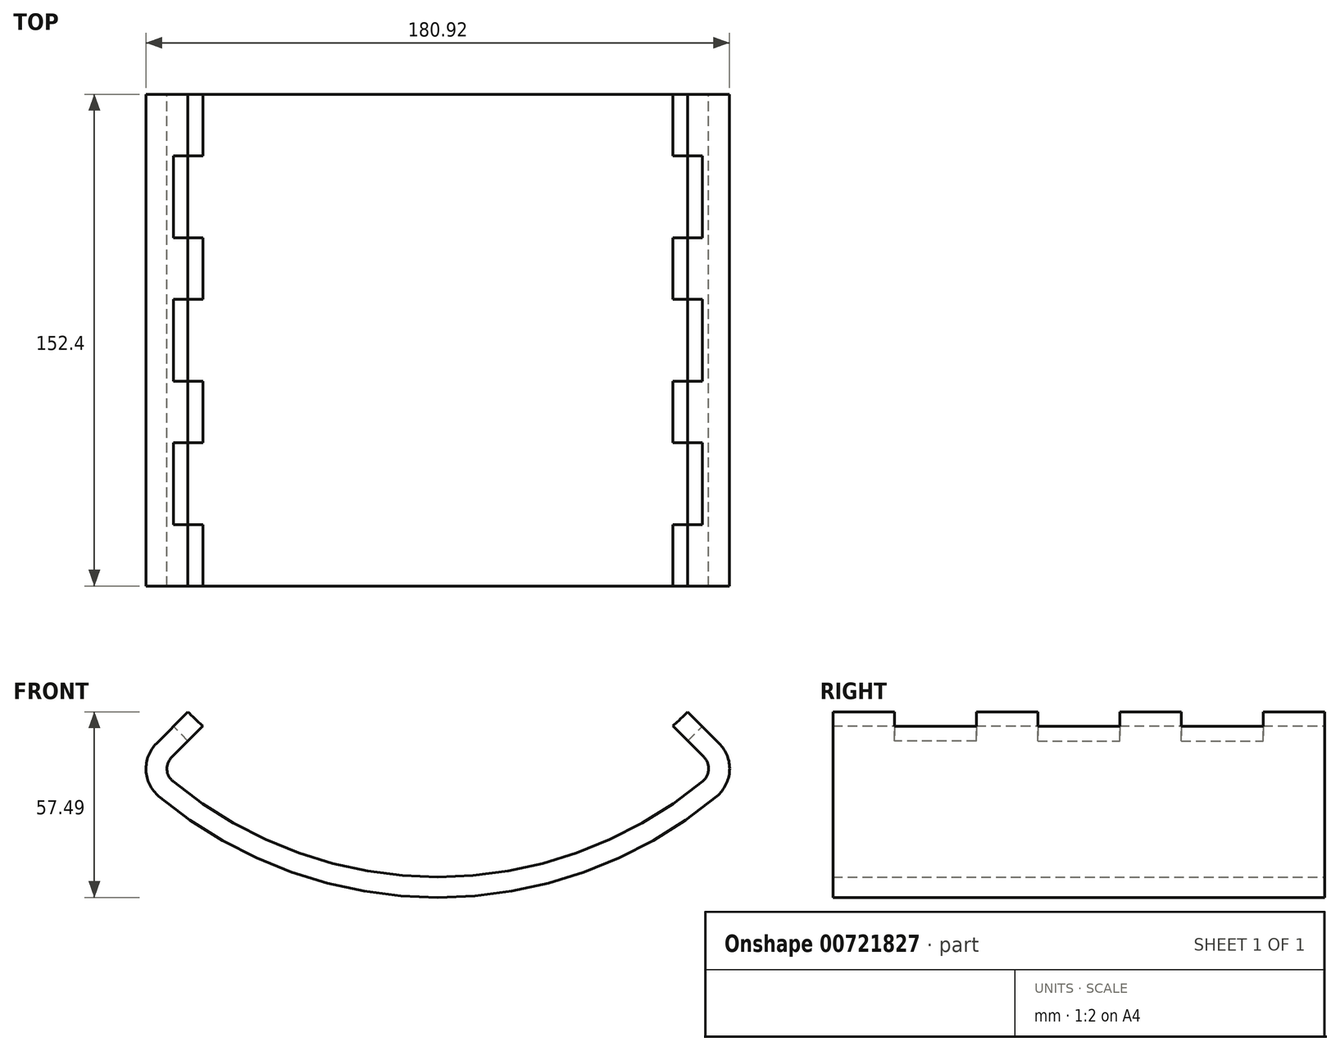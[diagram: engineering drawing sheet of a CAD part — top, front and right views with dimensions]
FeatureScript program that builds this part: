
annotation { "Feature Type Name" : "Feature", "Feature Type Description" : "" }
export const myFeature = defineFeature(function(context is Context, id is Id, definition is map)
    precondition{}
    {
        {
            var Q0;
            Q0=qCreatedBy(makeId("Front.planeOp"),FACE);
            var sketch = newSketch(context, id + "F0", { "sketchPlane" : qUnion([Q0])});
            skArc(sketch, "E0", {"start": v(-85.5, -96.04) * mm, "mid": v(0, -128.59) * mm, "end": v(85.5, -96.04) * mm});
            skArc(sketch, "E1", {"start": v(-95.42, -95.42) * mm, "mid": v(0, -134.94) * mm, "end": v(95.42, -95.42) * mm});
            skArc(sketch, "E2", {"start": v(-77.45, -77.45) * mm, "mid": v(-75.18, -79.67) * mm, "end": v(-72.83, -81.81) * mm});
            skArc(sketch, "E3.trimOffspring", {"start": v(72.83, -81.81) * mm, "mid": v(75.35, -79.5) * mm, "end": v(77.79, -77.12) * mm});
            skLineSegment(sketch, "E4", {"start": v(-77.45, -77.45) * mm, "end": v(-95.42, -95.42) * mm});
            skLineSegment(sketch, "E5", {"start": v(-72.83, -81.81) * mm, "end": v(-86.32, -95.3) * mm});
            skLineSegment(sketch, "E6", {"start": v(72.83, -81.81) * mm, "end": v(86.32, -95.3) * mm});
            skLineSegment(sketch, "E7", {"start": v(77.45, -77.45) * mm, "end": v(95.42, -95.42) * mm});
            skArc(sketch, "E8", {"start": v(-86.32, -95.3) * mm, "mid": v(0, -128.59) * mm, "end": v(86.32, -95.3) * mm});
            skArc(sketch, "E9.trimOffspring", {"start": v(-91.03, -90.82) * mm, "mid": v(-90.98, -90.87) * mm, "end": v(-90.93, -90.93) * mm});
            skSolve(sketch);
        }
        {
            var Q0;
            Q0 = qSketchRegion(id + "F0", true);
            extrude(context, id + "F1", {"entities" : qUnion([Q0]), "depth" : 152.4 * mm, "offsetDistance" : 25.4 * mm, "symmetric" : true});
        }
        {
            var Q0;
            Q0=makeQuery(id+"F1.opExtrude","SWEPT_EDGE",EDGE,{"disambiguationData":[OSD([sQuery(id+"F0.wireOp",EDGE,"E1"),sQuery(id+"F0.wireOp",EDGE,"b23c7c19-87c6-4823-a1c1-1b1030b646d8.trimOffspring")])]});
            var Q1;
            Q1=makeQuery(id+"F1.opExtrude","SWEPT_EDGE",EDGE,{"disambiguationData":[OSD([sQuery(id+"F0.wireOp",EDGE,"E1"),sQuery(id+"F0.wireOp",EDGE,"43c429cb-6016-4fc4-948b-cda1806fe1c8.trimOffspring")])]});
            fillet(context, id + "F2", {"entities" : qUnion([Q0, Q1]), "radius" : 11.1 * mm, "tangentPropagation" : true, "allowEdgeOverflow" : false});
        }
        {
            var Q0;
            Q0=makeQuery(id+"F1.opExtrude","SWEPT_EDGE",EDGE,{"disambiguationData":[OSD([sQuery(id+"F0.wireOp",EDGE,"E5"),sQuery(id+"F0.wireOp",EDGE,"E8")])]});
            var Q1;
            Q1=makeQuery(id+"F1.opExtrude","SWEPT_EDGE",EDGE,{"disambiguationData":[OSD([sQuery(id+"F0.wireOp",EDGE,"E6"),sQuery(id+"F0.wireOp",EDGE,"E8")])]});
            fillet(context, id + "F3", {"entities" : qUnion([Q0, Q1]), "radius" : 5.08 * mm, "tangentPropagation" : true, "allowEdgeOverflow" : false});
        }
        {
            var Q0;
            Q0=makeQuery(id+"F1.opExtrude","SWEPT_FACE",FACE,{"disambiguationData":[OSD([sQuery(id+"F0.wireOp",EDGE,"E7")])]});
            var sketch = newSketch(context, id + "F4", { "sketchPlane" : qUnion([Q0])});
            skLineSegment(sketch, "E10.bottom", {"start": v(-57.15, -106.28) * mm, "end": v(-31.75, -106.28) * mm});
            skLineSegment(sketch, "E10.top", {"start": v(-57.15, -115.89) * mm, "end": v(-31.75, -115.89) * mm});
            skLineSegment(sketch, "E10.left", {"start": v(-57.15, -106.28) * mm, "end": v(-57.15, -115.89) * mm});
            skLineSegment(sketch, "E10.right", {"start": v(-31.75, -106.28) * mm, "end": v(-31.75, -115.89) * mm});
            skLineSegment(sketch, "E11.MirrorCS", {"start": v(31.75, -106.28) * mm, "end": v(31.75, -115.89) * mm});
            skLineSegment(sketch, "E12.MirrorCS", {"start": v(57.15, -106.28) * mm, "end": v(31.75, -106.28) * mm});
            skLineSegment(sketch, "E13.MirrorCS", {"start": v(57.15, -115.89) * mm, "end": v(31.75, -115.89) * mm});
            skLineSegment(sketch, "E14.MirrorCS", {"start": v(57.15, -106.28) * mm, "end": v(57.15, -115.89) * mm});
            skLineSegment(sketch, "E15.bottom", {"start": v(-12.7, -105.34) * mm, "end": v(12.7, -105.34) * mm});
            skLineSegment(sketch, "E15.top", {"start": v(-12.7, -115.89) * mm, "end": v(12.7, -115.89) * mm});
            skLineSegment(sketch, "E15.left", {"start": v(-12.7, -105.34) * mm, "end": v(-12.7, -115.89) * mm});
            skLineSegment(sketch, "E15.right", {"start": v(12.7, -105.34) * mm, "end": v(12.7, -115.89) * mm});
            skSolve(sketch);
        }
        {
            var Q0;
            Q0 = qSketchRegion(id + "F4", true);
            extrude(context, id + "F5", {"entities" : qUnion([Q0]), "operationType" : NewBodyOperationType.REMOVE, "oppositeDirection" : true, "depth" : 25.4 * mm, "offsetDistance" : 25.4 * mm});
        }
        {
            var Q0;
            Q0=makeQuery(id+"F1.opExtrude","SWEPT_FACE",FACE,{"disambiguationData":[OSD([sQuery(id+"F0.wireOp",EDGE,"E4")])]});
            var sketch = newSketch(context, id + "F6", { "sketchPlane" : qUnion([Q0])});
            skLineSegment(sketch, "E16.bottom", {"start": v(-57.15, -103.22) * mm, "end": v(-31.75, -103.22) * mm});
            skLineSegment(sketch, "E16.top", {"start": v(-57.15, -115.89) * mm, "end": v(-31.75, -115.89) * mm});
            skLineSegment(sketch, "E16.left", {"start": v(-57.15, -103.22) * mm, "end": v(-57.15, -115.89) * mm});
            skLineSegment(sketch, "E16.right", {"start": v(-31.75, -103.22) * mm, "end": v(-31.75, -115.89) * mm});
            skLineSegment(sketch, "E17.MirrorCS", {"start": v(31.75, -103.22) * mm, "end": v(31.75, -115.89) * mm});
            skLineSegment(sketch, "E18.MirrorCS", {"start": v(57.15, -103.22) * mm, "end": v(31.75, -103.22) * mm});
            skLineSegment(sketch, "E19.MirrorCS", {"start": v(57.15, -115.89) * mm, "end": v(31.75, -115.89) * mm});
            skLineSegment(sketch, "E20.MirrorCS", {"start": v(57.15, -103.22) * mm, "end": v(57.15, -115.89) * mm});
            skLineSegment(sketch, "E21.bottom", {"start": v(-12.7, -100.5) * mm, "end": v(12.7, -100.5) * mm});
            skLineSegment(sketch, "E21.top", {"start": v(-12.7, -115.89) * mm, "end": v(12.7, -115.89) * mm});
            skLineSegment(sketch, "E21.left", {"start": v(-12.7, -100.5) * mm, "end": v(-12.7, -115.89) * mm});
            skLineSegment(sketch, "E21.right", {"start": v(12.7, -100.5) * mm, "end": v(12.7, -115.89) * mm});
            skSolve(sketch);
        }
        {
            var Q0;
            Q0 = qSketchRegion(id + "F6", true);
            extrude(context, id + "F7", {"entities" : qUnion([Q0]), "operationType" : NewBodyOperationType.REMOVE, "oppositeDirection" : true, "depth" : 25.4 * mm, "offsetDistance" : 25.4 * mm});
        }
    });
